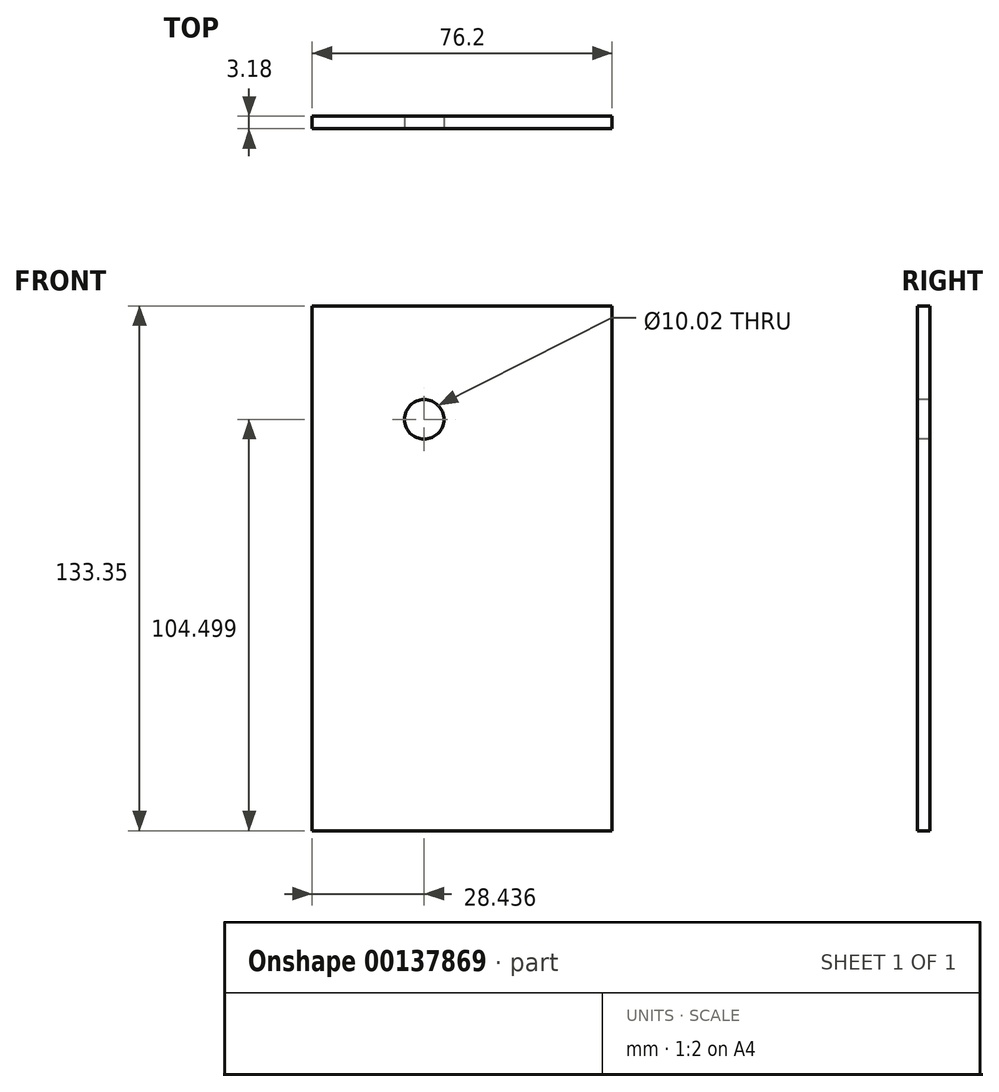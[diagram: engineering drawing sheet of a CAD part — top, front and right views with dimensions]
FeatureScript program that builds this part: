
annotation { "Feature Type Name" : "Feature", "Feature Type Description" : "" }
export const myFeature = defineFeature(function(context is Context, id is Id, definition is map)
    precondition{}
    {
        {
            var Q0;
            Q0=qCreatedBy(makeId("Front.planeOp"),FACE);
            var sketch = newSketch(context, id + "F0", { "sketchPlane" : qUnion([Q0])});
            skLineSegment(sketch, "E0.bottom", {"start": v(-79.82, 67.12) * mm, "end": v(-3.62, 67.12) * mm});
            skLineSegment(sketch, "E0.top", {"start": v(-79.82, -66.23) * mm, "end": v(-3.62, -66.23) * mm});
            skLineSegment(sketch, "E0.left", {"start": v(-79.82, 67.12) * mm, "end": v(-79.82, -66.23) * mm});
            skLineSegment(sketch, "E0.right", {"start": v(-3.62, 67.12) * mm, "end": v(-3.62, -66.23) * mm});
            skSolve(sketch);
        }
        {
            var Q0;
            Q0 = qSketchRegion(id + "F0", true);
            extrude(context, id + "F1", {"entities" : qUnion([Q0]), "depth" : 3.17 * mm});
        }
        {
            var Q0;
            Q0=makeQuery(id+"F1.opExtrude","CAP_FACE",FACE,{"disambiguationData":[OSD([sQuery(id+"F0.wireOp",EDGE,"E0.bottom"),sQuery(id+"F0.wireOp",EDGE,"E0.top"),sQuery(id+"F0.wireOp",EDGE,"E0.left"),sQuery(id+"F0.wireOp",EDGE,"E0.right")])],"isStart":false});
            var sketch = newSketch(context, id + "F2", { "sketchPlane" : qUnion([Q0])});
            skCircle(sketch, "E1", {"center": v(-51.38, 38.27) * mm, "radius": 5.01 * mm});
            skSolve(sketch);
        }
        {
            var Q0;
            Q0 = qSketchRegion(id + "F2", true);
            extrude(context, id + "F3", {"entities" : qUnion([Q0]), "operationType" : NewBodyOperationType.REMOVE, "endBound" : BoundingType.THROUGH_ALL, "oppositeDirection" : true, "depth" : 25.4 * mm});
        }
    });
